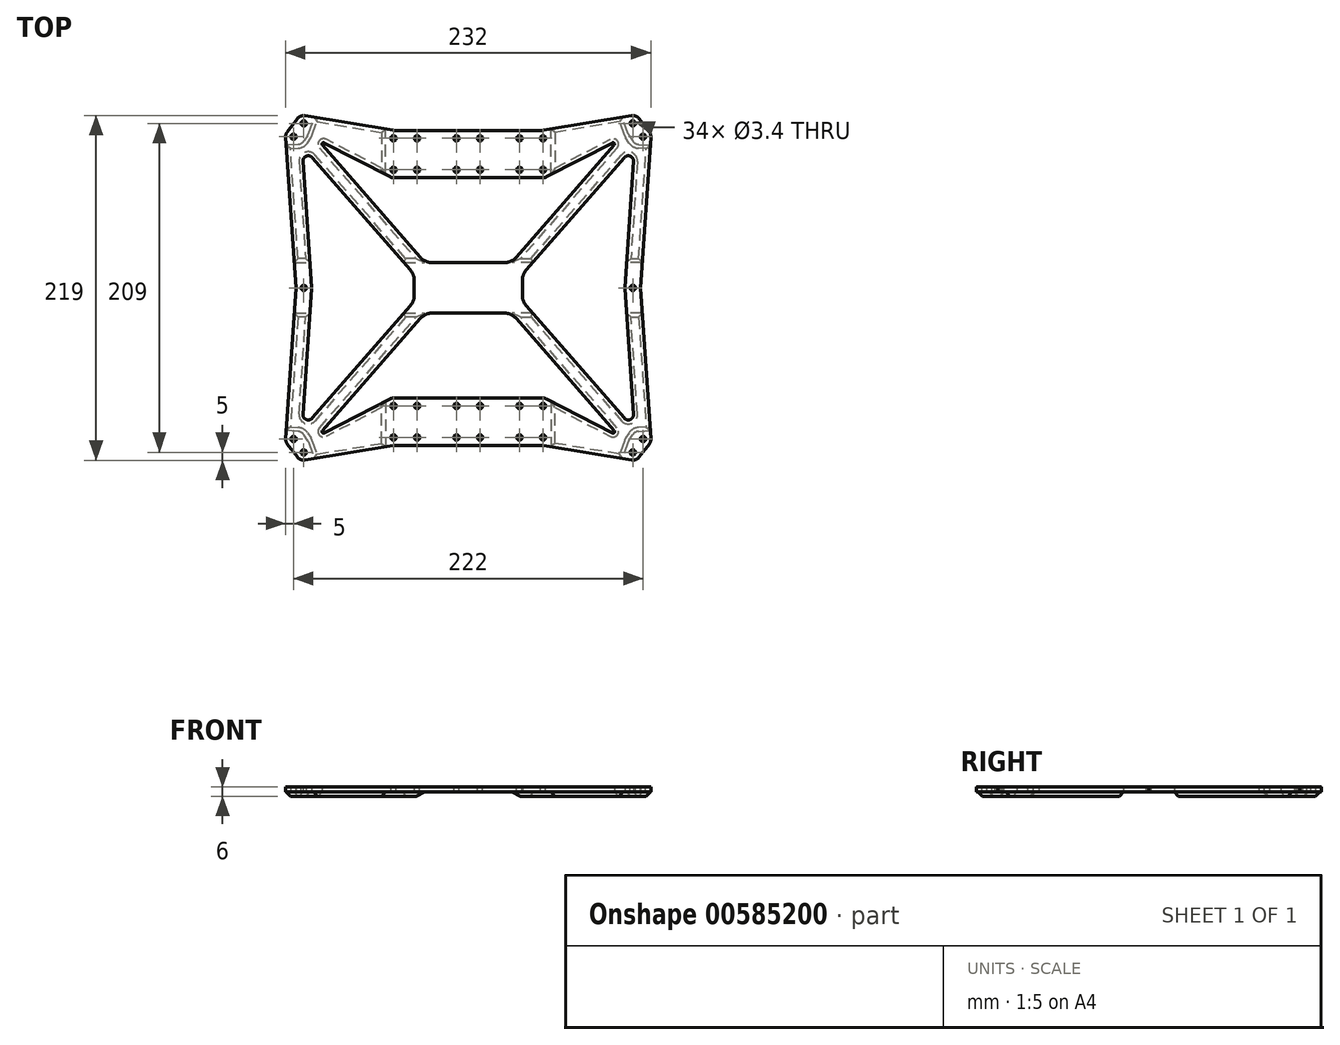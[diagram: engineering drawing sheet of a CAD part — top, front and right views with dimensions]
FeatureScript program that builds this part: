
annotation { "Feature Type Name" : "Feature", "Feature Type Description" : "" }
export const myFeature = defineFeature(function(context is Context, id is Id, definition is map)
    precondition{}
    {
        {
            var Q0;
            Q0=qCreatedBy(makeId("Top.planeOp"),FACE);
            var sketch = newSketch(context, id + "F0", { "sketchPlane" : qUnion([Q0])});
            skCircle(sketch, "E0", {"center": v(-47.5, -75) * mm, "radius": 1.6 * mm});
            skCircle(sketch, "E1.0.1.0", {"center": v(-47.5, -95) * mm, "radius": 1.6 * mm});
            skCircle(sketch, "E1.1.0.0", {"center": v(-32.5, -75) * mm, "radius": 1.6 * mm});
            skCircle(sketch, "E1.1.1.0", {"center": v(-32.5, -95) * mm, "radius": 1.6 * mm});
            skLineSegment(sketch, "E1.direction1", {"start": v(-47.5, -75) * mm, "end": v(-32.5, -75) * mm, "construction": true});
            skLineSegment(sketch, "E1.direction2", {"start": v(-47.5, -75) * mm, "end": v(-47.5, -95) * mm, "construction": true});
            skCircle(sketch, "E2.0.1.0", {"center": v(-7.49, 95) * mm, "radius": 1.6 * mm});
            skCircle(sketch, "E2.0.1.1", {"center": v(7.51, 95) * mm, "radius": 1.6 * mm});
            skCircle(sketch, "E2.0.1.2", {"center": v(-7.49, 75) * mm, "radius": 1.6 * mm});
            skCircle(sketch, "E2.0.1.3", {"center": v(7.51, 75) * mm, "radius": 1.6 * mm});
            skCircle(sketch, "E2.1.0.0", {"center": v(32.5, -75) * mm, "radius": 1.6 * mm});
            skCircle(sketch, "E2.1.0.1", {"center": v(47.5, -75) * mm, "radius": 1.6 * mm});
            skCircle(sketch, "E2.1.0.2", {"center": v(32.5, -95) * mm, "radius": 1.6 * mm});
            skCircle(sketch, "E2.1.0.3", {"center": v(47.5, -95) * mm, "radius": 1.6 * mm});
            skLineSegment(sketch, "E2.direction1", {"start": v(-47.5, -75) * mm, "end": v(32.5, -75) * mm, "construction": true});
            skLineSegment(sketch, "E2.direction2", {"start": v(-47.5, -75) * mm, "end": v(-47.5, 95) * mm, "construction": true});
            skLineSegment(sketch, "E3", {"start": v(-47.6, 95) * mm, "end": v(-7.6, 95) * mm, "construction": true});
            skPoint(sketch, "E4", {"position": v(7.5, -75) * mm});
            skPoint(sketch, "E5", {"position": v(-7.5, -75) * mm});
            skPoint(sketch, "E6", {"position": v(-7.5, -95) * mm});
            skPoint(sketch, "E7", {"position": v(7.5, -95) * mm});
            skPoint(sketch, "E8", {"position": v(47.5, 75) * mm});
            skPoint(sketch, "E9", {"position": v(47.5, 95) * mm});
            skPoint(sketch, "E10", {"position": v(32.5, 95) * mm});
            skPoint(sketch, "E11", {"position": v(-47.5, 75) * mm});
            skPoint(sketch, "E12", {"position": v(-32.5, 95) * mm});
            skLineSegment(sketch, "E13", {"start": v(-47.5, 95) * mm, "end": v(47.5, -95) * mm, "construction": true});
            skPoint(sketch, "E14", {"position": v(0, 0) * mm});
            skLineSegment(sketch, "E15.bottom", {"start": v(104.5, -104.5) * mm, "end": v(-104.5, -104.5) * mm, "construction": true});
            skLineSegment(sketch, "E15.top", {"start": v(104.5, 104.5) * mm, "end": v(-104.5, 104.5) * mm, "construction": true});
            skLineSegment(sketch, "E15.left", {"start": v(104.5, -104.5) * mm, "end": v(104.5, 104.5) * mm, "construction": true});
            skLineSegment(sketch, "E15.right", {"start": v(-104.5, -104.5) * mm, "end": v(-104.5, 104.5) * mm, "construction": true});
            skPoint(sketch, "E16", {"position": v(-104.5, 104.5) * mm});
            skPoint(sketch, "E17", {"position": v(104.5, 104.5) * mm});
            skPoint(sketch, "E18", {"position": v(-104.5, -104.5) * mm});
            skPoint(sketch, "E19", {"position": v(104.5, -104.5) * mm});
            skLineSegment(sketch, "E20.bottom", {"start": v(111, -96) * mm, "end": v(-111, -96) * mm, "construction": true});
            skLineSegment(sketch, "E20.top", {"start": v(111, 96) * mm, "end": v(-111, 96) * mm, "construction": true});
            skLineSegment(sketch, "E20.left", {"start": v(111, -96) * mm, "end": v(111, 96) * mm, "construction": true});
            skLineSegment(sketch, "E20.right", {"start": v(-111, -96) * mm, "end": v(-111, 96) * mm, "construction": true});
            skPoint(sketch, "E21", {"position": v(-111, 96) * mm});
            skPoint(sketch, "E22", {"position": v(111, 96) * mm});
            skPoint(sketch, "E23", {"position": v(111, -96) * mm});
            skPoint(sketch, "E24", {"position": v(-111, -96) * mm});
            skPoint(sketch, "E25", {"position": v(-104.5, 0) * mm});
            skPoint(sketch, "E26", {"position": v(104.5, 0) * mm});
            skPoint(sketch, "E27", {"position": v(32.5, 75) * mm});
            skPoint(sketch, "E28", {"position": v(-32.5, 75) * mm});
            skPoint(sketch, "E29", {"position": v(-47.5, 95) * mm});
            skSolve(sketch);
        }
        {
            var Q0;
            Q0=qCreatedBy(makeId("Top.planeOp"),FACE);
            var sketch = newSketch(context, id + "F1", { "sketchPlane" : qUnion([Q0])});
            skLineSegment(sketch, "E30.bottom", {"start": v(116, -109.5) * mm, "end": v(-116, -109.5) * mm});
            skLineSegment(sketch, "E30.top", {"start": v(116, 109.5) * mm, "end": v(-116, 109.5) * mm});
            skLineSegment(sketch, "E30.left", {"start": v(116, -109.5) * mm, "end": v(116, 109.5) * mm});
            skLineSegment(sketch, "E30.right", {"start": v(-116, -109.5) * mm, "end": v(-116, 109.5) * mm});
            skPoint(sketch, "E30.middle", {"position": v(0, 0) * mm});
            skSolve(sketch);
        }
        {
            var Q0;
            Q0=makeQuery(id+"F1.imprint","IMPRINT",FACE,{"disambiguationData":[TD([[makeQuery(id+"F1.imprint","IMPRINT",EDGE,{"derivedFrom":sQuery(id+"F1.wireOp",EDGE,"E30.bottom")}),-1.0]])]});
            extrude(context, id + "F2", {"entities" : qUnion([Q0]), "oppositeDirection" : true, "depth" : 6 * mm, "offsetDistance" : 25 * mm});
        }
        {
            var Q0;
            Q0=sQuery(id+"F0.wireOp",VERTEX,"E21");
            var Q1;
            Q1=sQuery(id+"F0.wireOp",VERTEX,"E16");
            var Q2;
            Q2=sQuery(id+"F0.wireOp",VERTEX,"E7");
            var Q3;
            Q3=sQuery(id+"F0.wireOp",VERTEX,"E6");
            var Q4;
            Q4=sQuery(id+"F0.wireOp",VERTEX,"E4");
            var Q5;
            Q5=sQuery(id+"F0.wireOp",VERTEX,"E5");
            var Q6;
            Q6=sQuery(id+"F0.wireOp",VERTEX,"E17");
            var Q7;
            Q7=sQuery(id+"F0.wireOp",VERTEX,"E22");
            var Q8;
            Q8=sQuery(id+"F0.wireOp",VERTEX,"E26");
            var Q9;
            Q9=sQuery(id+"F0.wireOp",VERTEX,"E23");
            var Q10;
            Q10=sQuery(id+"F0.wireOp",VERTEX,"E19");
            var Q11;
            Q11=sQuery(id+"F0.wireOp",VERTEX,"E2.1.0.3.center");
            var Q12;
            Q12=sQuery(id+"F0.wireOp",VERTEX,"E11");
            var Q13;
            Q13=sQuery(id+"F0.wireOp",VERTEX,"E2.1.0.0.center");
            var Q14;
            Q14=sQuery(id+"F0.wireOp",VERTEX,"E12");
            var Q15;
            Q15=sQuery(id+"F0.wireOp",VERTEX,"E10");
            var Q16;
            Q16=sQuery(id+"F0.wireOp",VERTEX,"E1.1.0.0.center");
            var Q17;
            Q17=sQuery(id+"F0.wireOp",VERTEX,"E8");
            var Q18;
            Q18=sQuery(id+"F0.wireOp",VERTEX,"E9");
            var Q19;
            Q19=sQuery(id+"F0.wireOp",VERTEX,"E18");
            var Q20;
            Q20=sQuery(id+"F0.wireOp",VERTEX,"E24");
            var Q21;
            Q21=sQuery(id+"F0.wireOp",VERTEX,"E25");
            var Q22;
            Q22=sQuery(id+"F0.wireOp",VERTEX,"E28");
            var Q23;
            Q23=sQuery(id+"F0.wireOp",VERTEX,"E29");
            var Q24;
            Q24=sQuery(id+"F0.wireOp",VERTEX,"E2.0.1.0.center");
            var Q25;
            Q25=sQuery(id+"F0.wireOp",VERTEX,"E2.0.1.1.center");
            var Q26;
            Q26=sQuery(id+"F0.wireOp",VERTEX,"E2.0.1.2.center");
            var Q27;
            Q27=sQuery(id+"F0.wireOp",VERTEX,"E2.0.1.3.center");
            var Q28;
            Q28=sQuery(id+"F0.wireOp",VERTEX,"E27");
            var Q29;
            Q29=sQuery(id+"F0.wireOp",VERTEX,"E0.center");
            var Q30;
            Q30=sQuery(id+"F0.wireOp",VERTEX,"E1.0.1.0.center");
            var Q31;
            Q31=sQuery(id+"F0.wireOp",VERTEX,"E1.1.1.0.center");
            var Q32;
            Q32=sQuery(id+"F0.wireOp",VERTEX,"E2.1.0.2.center");
            var Q33;
            Q33=sQuery(id+"F0.wireOp",VERTEX,"E2.1.0.1.center");
            var Q34;
            Q34=makeQuery(id+"F2.opExtrude","SWEPT_BODY",BODY,{"disambiguationData":[OSD([sQuery(id+"F1.wireOp",EDGE,"E30.bottom"),sQuery(id+"F1.wireOp",EDGE,"E30.top"),sQuery(id+"F1.wireOp",EDGE,"E30.left"),sQuery(id+"F1.wireOp",EDGE,"E30.right")])]});
            hole(context, id + "F3", {"style" : HoleStyle.SIMPLE, "endStyle" : HoleEndStyle.THROUGH, "holeDiameter" : 3.4 * mm, "majorDiameter" : 5 * mm, "isTappedThrough" : true, "tappedDepth" : 19 * mm, "tapClearance" : 0, "startFromSketch" : true, "locations" : qUnion([Q0, Q1, Q2, Q3, Q4, Q5, Q6, Q7, Q8, Q9, Q10, Q11, Q12, Q13, Q14, Q15, Q16, Q17, Q18, Q19, Q20, Q21, Q22, Q23, Q24, Q25, Q26, Q27, Q28, Q29, Q30, Q31, Q32, Q33]), "scope" : qUnion([Q34])});
        }
        {
            var Q0;
            Q0=makeQuery(id+"F2.opExtrude","CAP_FACE",FACE,{"disambiguationData":[OSD([sQuery(id+"F1.wireOp",EDGE,"E30.bottom"),sQuery(id+"F1.wireOp",EDGE,"E30.top"),sQuery(id+"F1.wireOp",EDGE,"E30.left"),sQuery(id+"F1.wireOp",EDGE,"E30.right")])],"isStart":false});
            var sketch = newSketch(context, id + "F4", { "sketchPlane" : qUnion([Q0])});
            skCircle(sketch, "E31", {"center": v(-47.5, -95) * mm, "radius": 5 * mm, "construction": true});
            skCircle(sketch, "E32", {"center": v(-32.5, -95) * mm, "radius": 5 * mm, "construction": true});
            skCircle(sketch, "E33", {"center": v(-7.49, -95) * mm, "radius": 5 * mm, "construction": true});
            skCircle(sketch, "E34", {"center": v(-7.49, -75) * mm, "radius": 5 * mm, "construction": true});
            skCircle(sketch, "E35", {"center": v(-32.5, -75) * mm, "radius": 5 * mm, "construction": true});
            skLineSegment(sketch, "E36", {"start": v(-109.5, 0) * mm, "end": v(-116, -95.83) * mm});
            skLineSegment(sketch, "E37", {"start": v(-114.97, -99.04) * mm, "end": v(-108.47, -107.54) * mm});
            skLineSegment(sketch, "E38", {"start": v(-47.5, -100) * mm, "end": v(-7.49, -100) * mm});
            skLineSegment(sketch, "E39", {"start": v(-46.68, -99.93) * mm, "end": v(-103.68, -109.43) * mm});
            skLineSegment(sketch, "E40", {"start": v(-7.49, -70) * mm, "end": v(-47.5, -70) * mm});
            skLineSegment(sketch, "E41", {"start": v(-49.8, -70.56) * mm, "end": v(-106.8, -100.06) * mm});
            skLineSegment(sketch, "E42", {"start": v(-99.51, -0.34) * mm, "end": v(-106.01, -96.34) * mm});
            skLineSegment(sketch, "E43", {"start": v(-100.53, -101.46) * mm, "end": v(-107.03, -92.96) * mm});
            skLineSegment(sketch, "E44.bottom", {"start": v(29.32, -11.07) * mm, "end": v(-29.32, -11.08) * mm, "construction": true});
            skLineSegment(sketch, "E44.top", {"start": v(29.32, 11.08) * mm, "end": v(-29.32, 11.07) * mm, "construction": true});
            skLineSegment(sketch, "E44.left", {"start": v(29.33, -11.07) * mm, "end": v(29.32, 11.08) * mm, "construction": true});
            skLineSegment(sketch, "E44.right", {"start": v(-29.32, -11.08) * mm, "end": v(-29.32, 11.07) * mm, "construction": true});
            skPoint(sketch, "E44.middle", {"position": v(0, 0) * mm});
            skLineSegment(sketch, "E45", {"start": v(-7.49, -70) * mm, "end": v(0, -70) * mm});
            skLineSegment(sketch, "E46", {"start": v(-7.49, -100) * mm, "end": v(0, -100) * mm});
            skLineSegment(sketch, "E47", {"start": v(-116, 0) * mm, "end": v(0, 0) * mm});
            skLineSegment(sketch, "E48", {"start": v(0, 0) * mm, "end": v(0, -109.5) * mm});
            skArc(sketch, "E49", {"start": v(-49.8, -70.56) * mm, "mid": v(-46.32, -79.86) * mm, "end": v(-47.5, -70) * mm, "construction": true});
            skArc(sketch, "E50", {"start": v(-47.5, -70) * mm, "mid": v(-48.68, -70.14) * mm, "end": v(-49.8, -70.56) * mm});
            skArc(sketch, "E51", {"start": v(-114.97, -99.04) * mm, "mid": v(-106.21, -94.56) * mm, "end": v(-115.99, -95.66) * mm, "construction": true});
            skArc(sketch, "E52", {"start": v(-115.99, -95.66) * mm, "mid": v(-115.79, -97.44) * mm, "end": v(-114.97, -99.04) * mm});
            skArc(sketch, "E53", {"start": v(-108.47, -107.54) * mm, "mid": v(-106.34, -109.15) * mm, "end": v(-103.68, -109.43) * mm});
            skArc(sketch, "E54", {"start": v(-103.68, -109.43) * mm, "mid": v(-102.66, -99.85) * mm, "end": v(-108.47, -107.54) * mm, "construction": true});
            skArc(sketch, "E55", {"start": v(-99.51, -0.34) * mm, "mid": v(-99.5, -0.17) * mm, "end": v(-99.5, 0) * mm});
            skArc(sketch, "E56", {"start": v(-109.5, 0) * mm, "mid": v(-104.67, -5) * mm, "end": v(-99.51, -0.34) * mm, "construction": true});
            skArc(sketch, "E57", {"start": v(-99.5, 0) * mm, "mid": v(-104.5, 5) * mm, "end": v(-109.5, 0) * mm, "construction": true});
            skLineSegment(sketch, "E58", {"start": v(-34.32, 0) * mm, "end": v(-34.32, -16.08) * mm});
            skLineSegment(sketch, "E59", {"start": v(-34.32, -16.08) * mm, "end": v(0, -16.07) * mm});
            skLineSegment(sketch, "E60", {"start": v(-52.5, -71.96) * mm, "end": v(-52.5, -100.9) * mm});
            skLineSegment(sketch, "E61", {"start": v(-101.67, -97.4) * mm, "end": v(-97.83, -108.46) * mm});
            skLineSegment(sketch, "E62", {"start": v(-105.67, -91.35) * mm, "end": v(-115.65, -90.67) * mm});
            skLineSegment(sketch, "E63", {"start": v(-104.5, -104.5) * mm, "end": v(-52.5, -86.43) * mm, "construction": true});
            skLineSegment(sketch, "E64", {"start": v(-104.5, -104.5) * mm, "end": v(-111, -96) * mm, "construction": true});
            skLineSegment(sketch, "E65", {"start": v(-107.75, -100.25) * mm, "end": v(-34.33, -16.08) * mm, "construction": true});
            skLineSegment(sketch, "E66", {"start": v(-27.7, -16.07) * mm, "end": v(-96.13, -94.54) * mm});
            skLineSegment(sketch, "E67", {"start": v(-34.32, -8.47) * mm, "end": v(-105.6, -90.17) * mm});
            skLineSegment(sketch, "E68", {"start": v(-101.67, -97.4) * mm, "end": v(-105.67, -91.35) * mm});
            skLineSegment(sketch, "E69", {"start": v(-110.6, -16.08) * mm, "end": v(-100.58, -16.08) * mm});
            skLineSegment(sketch, "E70", {"start": v(-40.96, -16.08) * mm, "end": v(-27.7, -16.08) * mm});
            skLineSegment(sketch, "E71", {"start": v(-34.32, -16.08) * mm, "end": v(-110.6, -16.08) * mm, "construction": true});
            skSolve(sketch);
        }
        {
            var Q0;
            {var subQ3=sQuery(id+"F1.wireOp",EDGE,"E30.bottom");var subQ35=makeQuery(id+"F2.opExtrude","CAP_EDGE",EDGE,{"disambiguationData":[OSD([subQ3])],"isStart":false});Q0=makeQuery(id+"F4.imprint","IMPRINT",FACE,{"disambiguationData":[TD([[makeQuery(id+"F4.imprint","IMPRINT",EDGE,{"derivedFrom":subQ35}),1.0]])]});}
            extrude(context, id + "F5", {"entities" : qUnion([Q0]), "operationType" : NewBodyOperationType.REMOVE, "endBound" : BoundingType.THROUGH_ALL, "oppositeDirection" : true, "depth" : 25 * mm, "offsetDistance" : 25 * mm});
        }
        {
            var Q0;
            {var subQ1=sQuery(id+"F4.wireOp",EDGE,"E37");Q0=makeQuery(id+"F4.imprint","IMPRINT",FACE,{"disambiguationData":[TD([[makeQuery(id+"F4.imprint","IMPRINT",EDGE,{"derivedFrom":subQ1}),-1.0]])]});}
            var Q1;
            {var subQ7=sQuery(id+"F4.wireOp",EDGE,"E46");Q1=makeQuery(id+"F4.imprint","IMPRINT",FACE,{"disambiguationData":[TD([[makeQuery(id+"F4.imprint","IMPRINT",EDGE,{"derivedFrom":subQ7}),-1.0]])]});}
            var Q2;
            {var subQ0=sQuery(id+"F4.wireOp",EDGE,"E47");var subQ1=sQuery(id+"F4.wireOp",EDGE,"E36");var subQ2=makeQuery(id+"F4.imprint","INTERSECT",VERTEX,{"derivedFrom":[subQ1,subQ0]});Q2=makeQuery(id+"F4.imprint","IMPRINT",FACE,{"disambiguationData":[TD([[makeQuery(id+"F4.imprint","IMPRINT",EDGE,{"disambiguationData":[TD([[subQ2,-1.0]])],"derivedFrom":subQ1}),-1.0]])]});}
            var Q3;
            {var subQ4=sQuery(id+"F4.wireOp",EDGE,"E55");Q3=makeQuery(id+"F4.imprint","IMPRINT",FACE,{"disambiguationData":[TD([[makeQuery(id+"F4.imprint","IMPRINT",EDGE,{"derivedFrom":subQ4}),-1.0]])]});}
            var Q4;
            Q4=makeQuery(id+"F4.imprint","IMPRINT",FACE,{"disambiguationData":[TD([[makeQuery(id+"F4.imprint","IMPRINT",EDGE,{"derivedFrom":sQuery(id+"F4.wireOp",EDGE,"E40")}),-1.0]])]});
            extrude(context, id + "F6", {"entities" : qUnion([Q0, Q1, Q2, Q3, Q4]), "operationType" : NewBodyOperationType.REMOVE, "endBound" : BoundingType.THROUGH_ALL, "oppositeDirection" : true, "depth" : 25 * mm, "offsetDistance" : 25 * mm});
        }
        {
            var Q0;
            {var subQ3=sQuery(id+"F4.wireOp",EDGE,"E58");Q0=makeQuery(id+"F4.imprint","IMPRINT",FACE,{"disambiguationData":[TD([[makeQuery(id+"F4.imprint","IMPRINT",EDGE,{"derivedFrom":subQ3}),1.0]])]});}
            var Q1;
            Q1=makeQuery(id+"F4.imprint","IMPRINT",FACE,{"disambiguationData":[TD([[makeQuery(id+"F4.imprint","IMPRINT",EDGE,{"derivedFrom":sQuery(id+"F4.wireOp",EDGE,"E40")}),1.0]])]});
            var Q2;
            {var subQ5=sQuery(id+"F4.wireOp",EDGE,"E37");Q2=makeQuery(id+"F4.imprint","IMPRINT",FACE,{"disambiguationData":[TD([[makeQuery(id+"F4.imprint","IMPRINT",EDGE,{"derivedFrom":subQ5}),1.0]])]});}
            var Q3;
            {var subQ0=sQuery(id+"F4.wireOp",EDGE,"E68");Q3=makeQuery(id+"F4.imprint","IMPRINT",FACE,{"disambiguationData":[TD([[makeQuery(id+"F4.imprint","IMPRINT",EDGE,{"derivedFrom":subQ0}),1.0]])]});}
            var Q4;
            {var subQ6=sQuery(id+"F4.wireOp",EDGE,"E55");Q4=makeQuery(id+"F4.imprint","IMPRINT",FACE,{"disambiguationData":[TD([[makeQuery(id+"F4.imprint","IMPRINT",EDGE,{"derivedFrom":subQ6}),1.0]])]});}
            var Q5;
            {var subQ1=sQuery(id+"F4.wireOp",EDGE,"E58");var subQ3=sQuery(id+"F4.wireOp",EDGE,"E67");var subQ4=makeQuery(id+"F4.imprint","INTERSECT",VERTEX,{"derivedFrom":[subQ1,subQ3]});Q5=makeQuery(id+"F4.imprint","IMPRINT",FACE,{"disambiguationData":[TD([[makeQuery(id+"F4.imprint","IMPRINT",EDGE,{"disambiguationData":[TD([[subQ4,-1.0]])],"derivedFrom":subQ3}),1.0]])]});}
            extrude(context, id + "F7", {"entities" : qUnion([Q0, Q1, Q2, Q3, Q4, Q5]), "operationType" : NewBodyOperationType.REMOVE, "oppositeDirection" : true, "depth" : 3 * mm, "offsetDistance" : 25 * mm});
        }
        {
            var Q0;
            {var subQ0=sQuery(id+"F4.wireOp",EDGE,"E59");var subQ1=sQuery(id+"F4.wireOp",EDGE,"E66");Q0=makeQuery(id+"F7.boolean.opBoolean","SPLIT",EDGE,{"disambiguationData":[topologyDisambiguationEdgeConnected([makeQuery(id+"F6.boolean.opBoolean","COPY",FACE,{"derivedFrom":makeQuery(id+"F6.opExtrude","SWEPT_FACE",FACE,{"disambiguationData":[OSD([subQ0])]})})])],"derivedFrom":makeQuery(id+"F6.boolean.opBoolean","COPY",EDGE,{"derivedFrom":makeQuery(id+"F6.opExtrude","SWEPT_EDGE",EDGE,{"disambiguationData":[OSD([subQ0,subQ1])]})})});}
            var Q1;
            {var subQ0=sQuery(id+"F4.wireOp",EDGE,"E58");var subQ1=sQuery(id+"F4.wireOp",EDGE,"E67");Q1=makeQuery(id+"F7.boolean.opBoolean","SPLIT",EDGE,{"disambiguationData":[topologyDisambiguationEdgeConnected([makeQuery(id+"F6.boolean.opBoolean","COPY",FACE,{"derivedFrom":makeQuery(id+"F6.opExtrude","SWEPT_FACE",FACE,{"disambiguationData":[OSD([subQ0])]})})])],"derivedFrom":makeQuery(id+"F6.boolean.opBoolean","COPY",EDGE,{"derivedFrom":makeQuery(id+"F6.opExtrude","SWEPT_EDGE",EDGE,{"disambiguationData":[OSD([subQ0,subQ1])]})})});}
            var Q2;
            Q2=makeQuery(id+"F6.boolean.opBoolean","COPY",EDGE,{"derivedFrom":makeQuery(id+"F6.opExtrude","SWEPT_EDGE",EDGE,{"disambiguationData":[OSD([sQuery(id+"F4.wireOp",EDGE,"E38"),sQuery(id+"F4.wireOp",EDGE,"E39")])]})});
            fillet(context, id + "F8", {"entities" : qUnion([Q0, Q1, Q2]), "radius" : 10 * mm, "tangentPropagation" : true, "allowEdgeOverflow" : false});
        }
        {
            var Q0;
            Q0=makeQuery(id+"F6.boolean.opBoolean","COPY",EDGE,{"derivedFrom":makeQuery(id+"F6.opExtrude","SWEPT_EDGE",EDGE,{"disambiguationData":[OSD([sQuery(id+"F4.wireOp",EDGE,"E41"),sQuery(id+"F4.wireOp",EDGE,"E66")])]})});
            fillet(context, id + "F9", {"entities" : qUnion([Q0]), "radius" : 1 * mm, "tangentPropagation" : true, "allowEdgeOverflow" : false});
        }
        {
            var Q0;
            Q0=makeQuery(id+"F6.boolean.opBoolean","COPY",EDGE,{"derivedFrom":makeQuery(id+"F6.opExtrude","SWEPT_EDGE",EDGE,{"disambiguationData":[OSD([sQuery(id+"F4.wireOp",EDGE,"E42"),sQuery(id+"F4.wireOp",EDGE,"E67")])]})});
            fillet(context, id + "F10", {"entities" : qUnion([Q0]), "radius" : 3.3 * mm, "tangentPropagation" : true, "allowEdgeOverflow" : false});
        }
        {
            var Q0;
            Q0=makeQuery(id+"F7.boolean.opBoolean","COPY",EDGE,{"derivedFrom":makeQuery(id+"F7.opExtrude","SWEPT_EDGE",EDGE,{"disambiguationData":[OSD([sQuery(id+"F4.wireOp",EDGE,"E42"),sQuery(id+"F4.wireOp",EDGE,"E62"),sQuery(id+"F4.wireOp",EDGE,"E68")])]})});
            var Q1;
            Q1=makeQuery(id+"F7.boolean.opBoolean","COPY",EDGE,{"derivedFrom":makeQuery(id+"F7.opExtrude","SWEPT_EDGE",EDGE,{"disambiguationData":[OSD([sQuery(id+"F4.wireOp",EDGE,"E41"),sQuery(id+"F4.wireOp",EDGE,"E61"),sQuery(id+"F4.wireOp",EDGE,"E68")])]})});
            var Q2;
            Q2=makeQuery(id+"F7.boolean.opBoolean","COPY",EDGE,{"derivedFrom":makeQuery(id+"F7.opExtrude","SWEPT_EDGE",EDGE,{"disambiguationData":[OSD([sQuery(id+"F4.wireOp",EDGE,"E39"),sQuery(id+"F4.wireOp",EDGE,"E61")])]})});
            var Q3;
            Q3=makeQuery(id+"F7.boolean.opBoolean","COPY",EDGE,{"derivedFrom":makeQuery(id+"F7.opExtrude","SWEPT_EDGE",EDGE,{"disambiguationData":[OSD([sQuery(id+"F4.wireOp",EDGE,"E36"),sQuery(id+"F4.wireOp",EDGE,"E62")])]})});
            var Q4;
            Q4=makeQuery(id+"F7.boolean.opBoolean","COPY",EDGE,{"derivedFrom":makeQuery(id+"F7.opExtrude","SWEPT_EDGE",EDGE,{"disambiguationData":[OSD([sQuery(id+"F4.wireOp",EDGE,"E39"),sQuery(id+"F4.wireOp",EDGE,"E60")])]})});
            var Q5;
            Q5=makeQuery(id+"F7.boolean.opBoolean","COPY",EDGE,{"derivedFrom":makeQuery(id+"F7.opExtrude","SWEPT_EDGE",EDGE,{"disambiguationData":[OSD([sQuery(id+"F4.wireOp",EDGE,"E41"),sQuery(id+"F4.wireOp",EDGE,"E60")])]})});
            fillet(context, id + "F11", {"entities" : qUnion([Q0, Q1, Q2, Q3, Q4, Q5]), "radius" : 5 * mm, "tangentPropagation" : true, "allowEdgeOverflow" : false});
        }
        {
            var Q0;
            Q0=makeQuery(id+"F2.opExtrude","CAP_FACE",FACE,{"disambiguationData":[OSD([sQuery(id+"F1.wireOp",EDGE,"E30.bottom"),sQuery(id+"F1.wireOp",EDGE,"E30.top"),sQuery(id+"F1.wireOp",EDGE,"E30.left"),sQuery(id+"F1.wireOp",EDGE,"E30.right")])],"isStart":false});
            chamfer(context, id + "F12", {"entities" : qUnion([Q0]), "chamferType" : ChamferType.OFFSET_ANGLE, "width" : 3 * mm, "oppositeDirection" : false, "angle" : 40 * degree, "tangentPropagation" : true});
        }
        {
            var Q0;
            Q0=makeQuery(id+"F2.opExtrude","SWEPT_BODY",BODY,{"disambiguationData":[OSD([sQuery(id+"F1.wireOp",EDGE,"E30.bottom"),sQuery(id+"F1.wireOp",EDGE,"E30.top"),sQuery(id+"F1.wireOp",EDGE,"E30.left"),sQuery(id+"F1.wireOp",EDGE,"E30.right")])]});
            var Q1;
            Q1=qCreatedBy(makeId("Right.planeOp"),FACE);
            mirror(context, id + "F13", {"operationType" : NewBodyOperationType.ADD, "entities" : qUnion([Q0]), "mirrorPlane" : qUnion([Q1])});
        }
        {
            var Q0;
            Q0=makeQuery(id+"F2.opExtrude","SWEPT_BODY",BODY,{"disambiguationData":[OSD([sQuery(id+"F1.wireOp",EDGE,"E30.bottom"),sQuery(id+"F1.wireOp",EDGE,"E30.top"),sQuery(id+"F1.wireOp",EDGE,"E30.left"),sQuery(id+"F1.wireOp",EDGE,"E30.right")])]});
            var Q1;
            Q1=qCreatedBy(makeId("Front.planeOp"),FACE);
            mirror(context, id + "F14", {"operationType" : NewBodyOperationType.ADD, "entities" : qUnion([Q0]), "mirrorPlane" : qUnion([Q1])});
        }
    });
